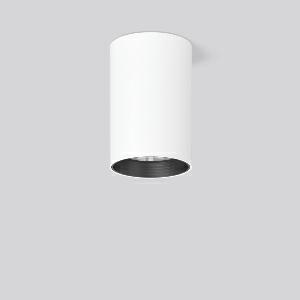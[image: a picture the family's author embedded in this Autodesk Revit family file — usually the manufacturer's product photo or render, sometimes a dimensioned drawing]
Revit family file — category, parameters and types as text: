
# Revit family: heledon_maxi_a_931222_002_1_d9bd
name_source: partatom
category: Lighting Fixtures
units: mm (PartAtom-declared; Revit-internal decimal feet)

## family parameters
Cut with Voids When Loaded = No
Host = Face
Light Source = No
Part Type = Normal
Room Calculation Point = No
Round Connector Dimension = Use Diameter
Shared = No

## types (1)
- HELEDON maxi A (1 x LED Modul 940, 2950 lm, 4000)
    Apparent Load = 25 VA
    Approval mark = CE
    CIE Flux Codes = 96 100 100 100 100
    Color Rendering = 92
    Color Temperature = 4000
    Default Elevation = 1800 mm
    Description = Series: HELEDON maxi
Cylindrical surface-mounted downlight. Housing: die-cast aluminium, powder-coated. Internal ceiling frame polycarbonate with bayonet mounting. Black plastic ring and recessed LED to prevent glare from the side. Optical assembly with lens made of plastic (polycarbonate) for the best homogeneous light distribution - can be changed without tools. Best colour rendering index Ra>90. Suitable for Ceiling mounting. Easy installation with a separate ceiling frame with bayonet mounting and plug connection. Driver integrated. Connected via plug-in connector. High quality converter without flickering and stroboscopic effect. The following accessories can be mounted without use of tools: interchangeable lenses, decorative glasses, honeycomb louvre, clear and frosted diffusers, white interchangeable plastic ring. 
Colour: traffic white, matt (RAL 9016)
Diameter: 123 mm
Height: 183 mm
Lamp: LED
Socket: without socket
Colour temperature: 4000K
Colour rendering index (CRI): 92
System power: 25 W
Rated luminous flux: 2950 lm
Luminous efficiency: 118 lm/W
Control gear: Regulated power supply
Protection class: I
Type of protection: IP 20
    Height = 183 mm
    Lamp = 1 x LED Modul 940
    Lamp Light Flux = 2950 lm
    Lamp count = 1
    Length = 123 mm
    Lifetime = 50000 h
    Luminous efficacy = 118 lm/W
    Manufacturer = RZB
    ModVariant = No
    Model = 931222.002.1
    Mounting Place = Ceiling
    Mounting Type = Surface mounted
    Number of Poles = 1
    OnlyDefault = Yes
    Power Factor = 1
    Product Name = HELEDON maxi A
    Product group = Surface mounted downlights
    ProductGroupID = 302
    Protection Class = Protection class I
    Protection Degree = IP 20
    RLX_Detail_Level = 1
    RLX_Emergency_Light_Flux = 0 lm
    RLX_Emergency_Type = 0
    RLX_Emergency_Type_DB = No
    RlxData = <blob elided: 97285 chars, md5=b6e5e1a7>
    Socket = socket
    Standby Power = 0 W
    System Light Flux = 2950 lm
    System Power = 25 W
    Type Comments = Product without accessories
    Type Image = 931193.002.jpg
    URL = http://relux.com
    VarID = ---
    Voltage = 230 V
    Voltage Range = 220-240 V
    Weight = 0.00 kg
    Width = 0 mm  [stored 0 ft]

note: [stored X ft] marks values corroborated as IEEE doubles in the binary element streams (Revit-internal decimal feet)

## geometry (parser evidence)
native form markers: Blend x4, Sweep x11
no freeform markers — native parametric forms only
